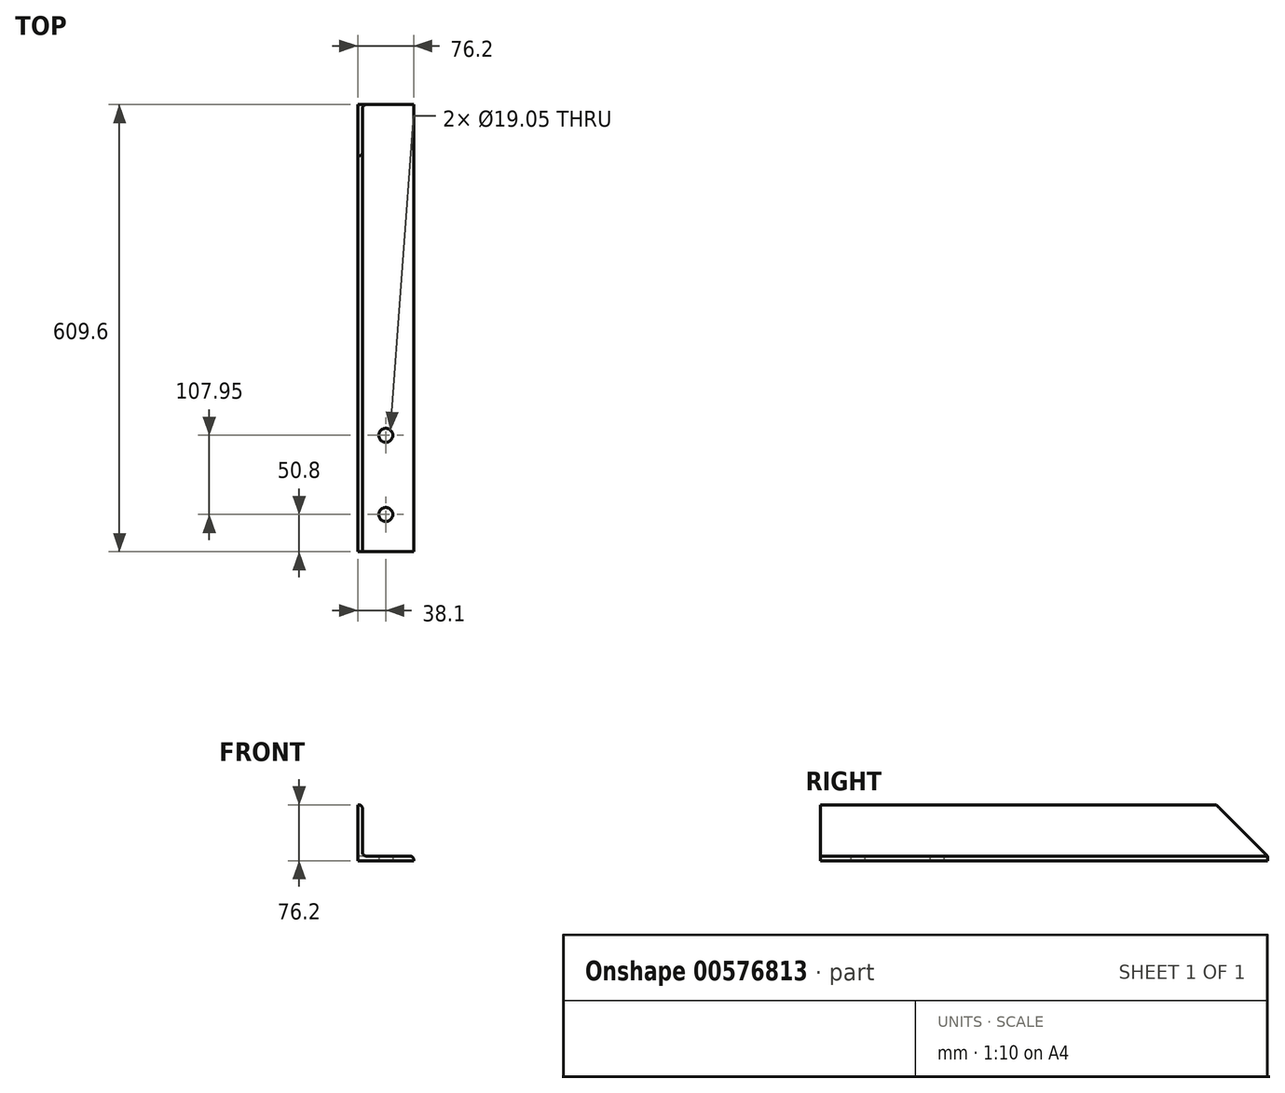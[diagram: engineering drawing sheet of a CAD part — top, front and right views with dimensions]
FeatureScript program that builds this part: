
annotation { "Feature Type Name" : "Feature", "Feature Type Description" : "" }
export const myFeature = defineFeature(function(context is Context, id is Id, definition is map)
    precondition{}
    {
        {
            var Q0;
            Q0=qCreatedBy(makeId("Front.planeOp"),FACE);
            var sketch = newSketch(context, id + "F0", { "sketchPlane" : qUnion([Q0])});
            skLineSegment(sketch, "E0", {"start": v(0, 0) * mm, "end": v(0, 76.2) * mm});
            skLineSegment(sketch, "E1", {"start": v(0, 76.2) * mm, "end": v(6.35, 76.2) * mm});
            skLineSegment(sketch, "E2", {"start": v(6.35, 76.2) * mm, "end": v(6.35, 6.35) * mm});
            skLineSegment(sketch, "E3", {"start": v(6.35, 6.35) * mm, "end": v(76.2, 6.35) * mm});
            skLineSegment(sketch, "E4", {"start": v(76.2, 6.35) * mm, "end": v(76.2, 0) * mm});
            skLineSegment(sketch, "E5", {"start": v(76.2, 0) * mm, "end": v(0, 0) * mm});
            skSolve(sketch);
        }
        {
            var Q0;
            Q0 = qSketchRegion(id + "F0", true);
            extrude(context, id + "F1", {"entities" : qUnion([Q0]), "endBound" : BoundingType.SYMMETRIC, "depth" : 609.6 * mm, "offsetDistance" : 25.4 * mm});
        }
        {
            var Q0;
            Q0=makeQuery(id+"F1.opExtrude","SWEPT_EDGE",EDGE,{"disambiguationData":[OSD([sQuery(id+"F0.wireOp",EDGE,"E1"),sQuery(id+"F0.wireOp",EDGE,"E2")])]});
            var Q1;
            Q1=makeQuery(id+"F1.opExtrude","SWEPT_EDGE",EDGE,{"disambiguationData":[OSD([sQuery(id+"F0.wireOp",EDGE,"E2"),sQuery(id+"F0.wireOp",EDGE,"E3")])]});
            var Q2;
            Q2=makeQuery(id+"F1.opExtrude","SWEPT_EDGE",EDGE,{"disambiguationData":[OSD([sQuery(id+"F0.wireOp",EDGE,"E3"),sQuery(id+"F0.wireOp",EDGE,"E4")])]});
            fillet(context, id + "F2", {"entities" : qUnion([Q0, Q1, Q2]), "radius" : 5.08 * mm, "tangentPropagation" : true, "allowEdgeOverflow" : false});
        }
        {
            var Q0;
            Q0=makeQuery(id+"F1.opExtrude","SWEPT_FACE",FACE,{"disambiguationData":[OSD([sQuery(id+"F0.wireOp",EDGE,"E0")])]});
            var sketch = newSketch(context, id + "F3", { "sketchPlane" : qUnion([Q0])});
            skPoint(sketch, "E6.0", {"position": v(-304.8, 6.35) * mm});
            skLineSegment(sketch, "E7", {"start": v(-304.8, 6.35) * mm, "end": v(-194.99, 116.16) * mm});
            skLineSegment(sketch, "E8", {"start": v(-194.99, 116.16) * mm, "end": v(-304.8, 116.16) * mm});
            skLineSegment(sketch, "E9", {"start": v(-304.8, 116.16) * mm, "end": v(-304.8, 6.35) * mm});
            skSolve(sketch);
        }
        {
            var Q0;
            Q0 = qSketchRegion(id + "F3", true);
            extrude(context, id + "F4", {"entities" : qUnion([Q0]), "operationType" : NewBodyOperationType.REMOVE, "oppositeDirection" : true, "depth" : 25.4 * mm, "offsetDistance" : 25.4 * mm});
        }
        {
            var Q0;
            Q0=makeQuery(id+"F1.opExtrude","SWEPT_FACE",FACE,{"disambiguationData":[OSD([sQuery(id+"F0.wireOp",EDGE,"E5")])]});
            var sketch = newSketch(context, id + "F5", { "sketchPlane" : qUnion([Q0])});
            skCircle(sketch, "E10", {"center": v(38.1, 254) * mm, "radius": 9.53 * mm});
            skCircle(sketch, "E11", {"center": v(38.1, 146.05) * mm, "radius": 9.53 * mm});
            skSolve(sketch);
        }
        {
            var Q0;
            Q0 = qSketchRegion(id + "F5", true);
            extrude(context, id + "F6", {"entities" : qUnion([Q0]), "operationType" : NewBodyOperationType.REMOVE, "oppositeDirection" : true, "depth" : 25.4 * mm, "offsetDistance" : 25.4 * mm});
        }
    });
